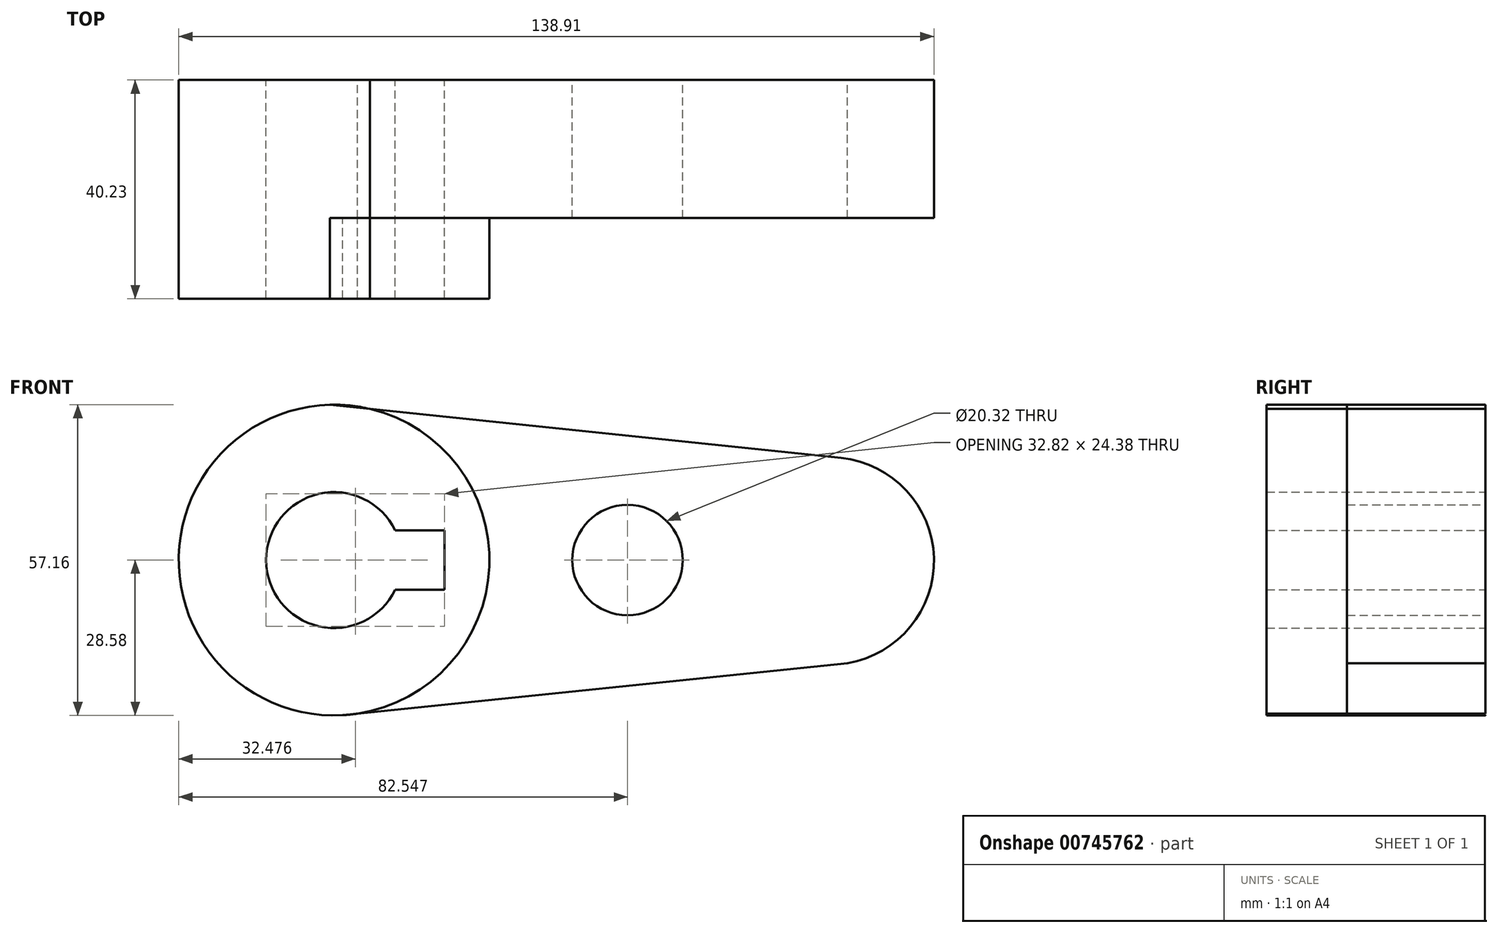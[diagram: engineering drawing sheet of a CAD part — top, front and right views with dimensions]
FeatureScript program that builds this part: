
annotation { "Feature Type Name" : "Feature", "Feature Type Description" : "" }
export const myFeature = defineFeature(function(context is Context, id is Id, definition is map)
    precondition{}
    {
        {
            var Q0;
            Q0=qCreatedBy(makeId("Front.planeOp"),FACE);
            var sketch = newSketch(context, id + "F0", { "sketchPlane" : qUnion([Q0])});
            skArc(sketch, "E0", {"start": v(-40.05, 11.7) * mm, "mid": v(-94.7, 0) * mm, "end": v(-40.05, -11.7) * mm});
            skCircle(sketch, "E1", {"center": v(-66.12, 0) * mm, "radius": 25.92 * mm});
            skCircle(sketch, "E2", {"center": v(-66.12, 0) * mm, "radius": 28.58 * mm});
            skCircle(sketch, "E3", {"center": v(-12.14, 0) * mm, "radius": 10.16 * mm});
            skLineSegment(sketch, "E4", {"start": v(-64.57, -28.53) * mm, "end": v(28.27, -18.96) * mm});
            skLineSegment(sketch, "E5", {"start": v(-66.87, 28.57) * mm, "end": v(27.14, 18.78) * mm});
            skArc(sketch, "E6", {"start": v(28.27, -18.96) * mm, "mid": v(44.2, 0.4) * mm, "end": v(27.14, 18.78) * mm});
            skLineSegment(sketch, "E7", {"start": v(-45.8, 2.02) * mm, "end": v(-45.8, 0) * mm});
            skArc(sketch, "E8", {"start": v(-54.86, 5.45) * mm, "mid": v(-78.56, 1.28) * mm, "end": v(-56.21, -7.63) * mm});
            skArc(sketch, "E9", {"start": v(-54.86, 5.45) * mm, "mid": v(-78.56, 1.28) * mm, "end": v(-56.21, -7.63) * mm, "construction": true});
            skLineSegment(sketch, "E10.bottom", {"start": v(-45.8, 5.45) * mm, "end": v(-54.86, 5.45) * mm});
            skLineSegment(sketch, "E10.top", {"start": v(-45.8, -5.45) * mm, "end": v(-54.86, -5.45) * mm});
            skLineSegment(sketch, "E10.left", {"start": v(-45.8, 5.45) * mm, "end": v(-45.8, -5.45) * mm});
            skPoint(sketch, "E10.middle", {"position": v(-53.61, 0) * mm});
            skPoint(sketch, "E11.orphan", {"position": v(-61.42, 5.45) * mm});
            skPoint(sketch, "E12.orphan", {"position": v(-61.42, -5.45) * mm});
            skArc(sketch, "E13", {"start": v(-56.21, -7.63) * mm, "mid": v(-55.48, -6.57) * mm, "end": v(-54.86, -5.45) * mm});
            skPoint(sketch, "E14.orphan", {"position": v(-53.78, 2.02) * mm});
            skSolve(sketch);
        }
        {
            var Q0;
            Q0 = qSketchRegion(id + "F0", true);
            extrude(context, id + "F1", {"entities" : qUnion([Q0]), "depth" : 25.4 * mm, "offsetDistance" : 25.4 * mm});
        }
        {
            var Q0;
            Q0=makeQuery(id+"F0.imprint","IMPRINT",FACE,{"disambiguationData":[TD([[makeQuery(id+"F0.imprint","IMPRINT",EDGE,{"derivedFrom":sQuery(id+"F0.wireOp",EDGE,"E1")}),1.0]])]});
            var Q1;
            Q1=makeQuery(id+"F0.imprint","IMPRINT",FACE,{"disambiguationData":[TD([[makeQuery(id+"F0.imprint","IMPRINT",EDGE,{"derivedFrom":sQuery(id+"F0.wireOp",EDGE,"E1")}),-1.0]])]});
            extrude(context, id + "F2", {"entities" : qUnion([Q0, Q1]), "depth" : 40.23 * mm, "offsetDistance" : 25.4 * mm});
        }
        {
            var Q0;
            Q0=makeQuery(id+"F0.imprint","IMPRINT",FACE,{"disambiguationData":[TD([[makeQuery(id+"F0.imprint","IMPRINT",EDGE,{"derivedFrom":sQuery(id+"F0.wireOp",EDGE,"E3")}),-1.0]])]});
            extrude(context, id + "F3", {"entities" : qUnion([Q0]), "operationType" : NewBodyOperationType.ADD, "depth" : 15.77 * mm, "offsetDistance" : 25.4 * mm});
        }
    });
